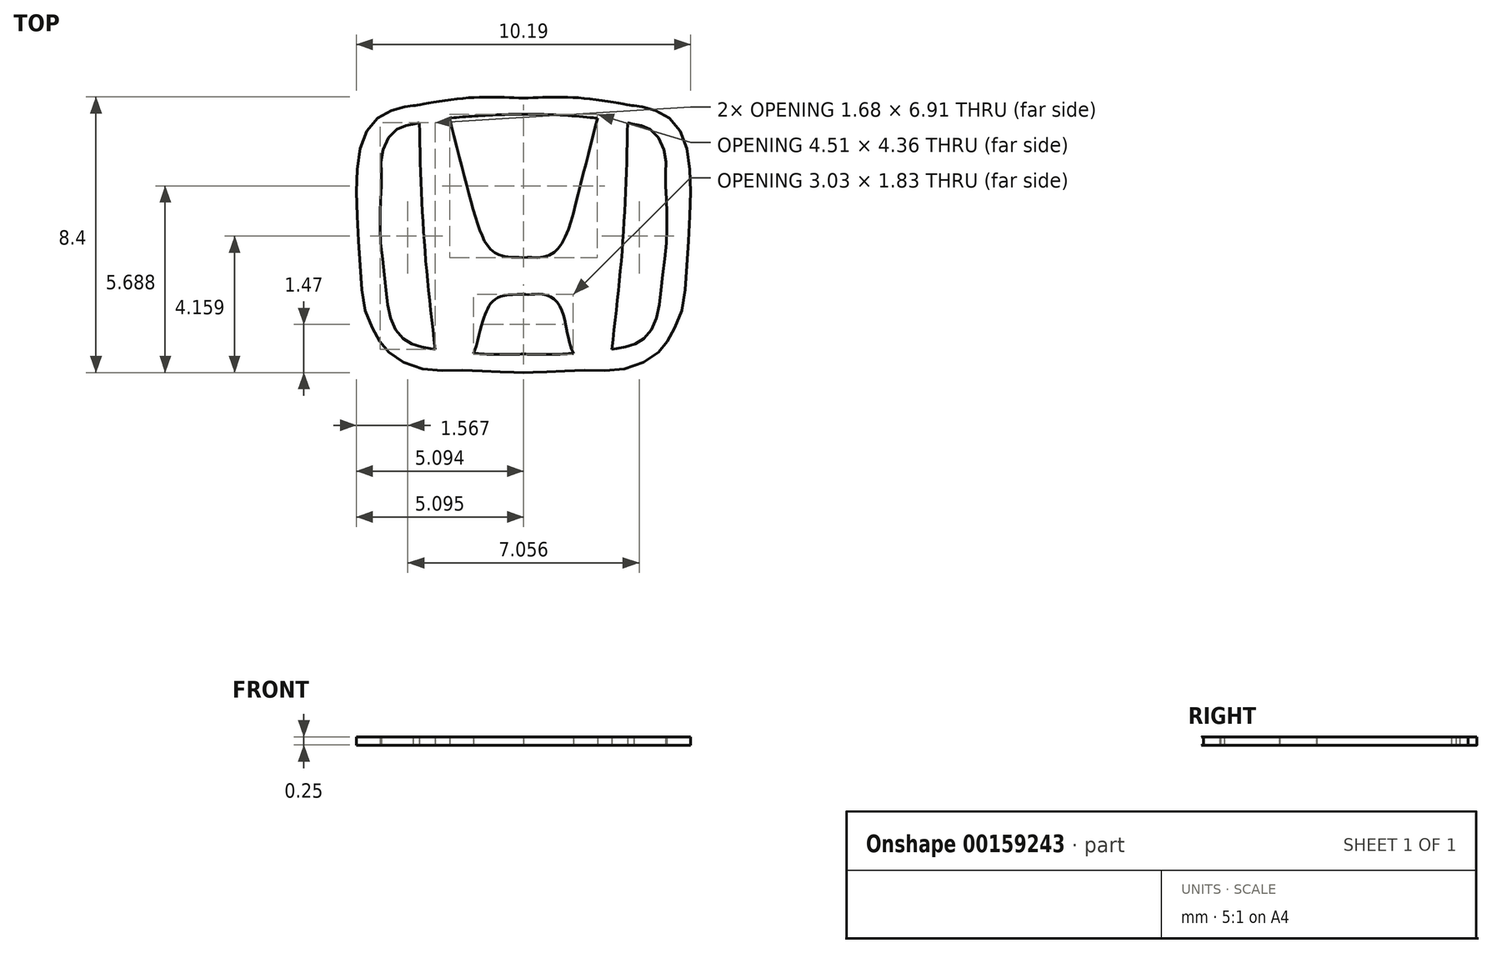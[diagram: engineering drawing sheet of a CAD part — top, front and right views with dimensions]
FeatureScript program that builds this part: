
annotation { "Feature Type Name" : "Feature", "Feature Type Description" : "" }
export const myFeature = defineFeature(function(context is Context, id is Id, definition is map)
    precondition{}
    {
        {
            var Q0;
            Q0=qCreatedBy(makeId("Top.planeOp"),FACE);
            var sketch = newSketch(context, id + "F0", { "sketchPlane" : qUnion([Q0])});
            skFitSpline(sketch, "E0.0", {"points": [v(1.68, -88.15) * mm, v(7.08, -88.08) * mm, v(18.75, -87.55) * mm, v(40.87, -86.74) * mm, v(64.03, -85.73) * mm, v(83.21, -76.44) * mm, v(90.57, -66.82) * mm, v(98.02, -50.85) * mm, v(101.38, -20.58) * mm, v(103.43, 15.7) * mm, v(101.94, 44.93) * mm, v(94.34, 63.37) * mm, v(81.86, 71.73) * mm, v(72.08, 74.1) * mm, v(68.98, 74.5) * mm]});
            skFitSpline(sketch, "E0.1", {"points": [v(65.18, 64.17) * mm, v(65.45, 64.1) * mm, v(70.48, 62.9) * mm, v(79.31, 60) * mm, v(87.76, 46.3) * mm, v(88.28, 32.38) * mm, v(88.84, 14.52) * mm, v(88.82, -7.63) * mm, v(85.9, -33.34) * mm, v(83.03, -54.06) * mm, v(75.44, -67.13) * mm, v(65.61, -72.1) * mm, v(58.1, -73.63) * mm, v(55.47, -74.06) * mm]});
            skFitSpline(sketch, "E0.2", {"points": [v(65.18, 64.17) * mm, v(63.78, 18) * mm, v(60.54, -28.08) * mm, v(55.47, -74.06) * mm]});
            skFitSpline(sketch, "E0.3", {"points": [v(1.68, -40.48) * mm, v(4.74, -40.57) * mm, v(11.56, -40.33) * mm, v(20.1, -43.16) * mm, v(26.16, -53.22) * mm, v(28.54, -64.7) * mm, v(30.94, -73.54) * mm, v(32.03, -76.46) * mm]});
            skFitSpline(sketch, "E0.4", {"points": [v(32.03, -76.46) * mm, v(21.9, -77) * mm, v(11.71, -77) * mm, v(1.68, -76.86) * mm]});
            skFitSpline(sketch, "E0.5", {"points": [v(1.68, -76.86) * mm, v(-8.35, -77) * mm, v(-18.53, -77) * mm, v(-28.67, -76.47) * mm]});
            skFitSpline(sketch, "E0.6", {"points": [v(-65.62, 74.5) * mm, v(-68.71, 74.1) * mm, v(-78.5, 71.73) * mm, v(-90.97, 63.37) * mm, v(-98.58, 44.93) * mm, v(-100.06, 15.7) * mm, v(-98, -20.58) * mm, v(-94.65, -50.85) * mm, v(-87.2, -66.82) * mm, v(-79.84, -76.44) * mm, v(-60.66, -85.73) * mm, v(-37.5, -86.74) * mm, v(-15.38, -87.55) * mm, v(-3.71, -88.08) * mm, v(1.68, -88.15) * mm]});
            skFitSpline(sketch, "E0.7", {"points": [v(1.68, -40.48) * mm, v(0.74, -40.5) * mm, v(-1.34, -40.52) * mm, v(-4.78, -40.58) * mm, v(-8.34, -40.87) * mm, v(-11.22, -41.45) * mm, v(-13.36, -42.2) * mm, v(-14.86, -42.94) * mm, v(-16.22, -43.86) * mm, v(-17.41, -45) * mm, v(-18.47, -46.3) * mm, v(-19.4, -47.74) * mm, v(-20.22, -49.25) * mm, v(-20.96, -50.8) * mm, v(-21.64, -52.36) * mm, v(-22.45, -54.47) * mm, v(-23.33, -57.13) * mm, v(-24.23, -60.35) * mm, v(-25.31, -64.67) * mm, v(-26.6, -70.09) * mm, v(-27.88, -74.36) * mm, v(-28.67, -76.47) * mm]});
            skFitSpline(sketch, "E0.8", {"points": [v(-52.1, -74.07) * mm, v(-57.18, -28.08) * mm, v(-60.41, 18) * mm, v(-61.8, 64.17) * mm]});
            skFitSpline(sketch, "E0.9", {"points": [v(-52.1, -74.07) * mm, v(-54.74, -73.63) * mm, v(-62.25, -72.1) * mm, v(-72.07, -67.13) * mm, v(-79.67, -54.06) * mm, v(-82.53, -33.34) * mm, v(-85.45, -7.63) * mm, v(-85.48, 14.52) * mm, v(-84.91, 32.38) * mm, v(-84.4, 46.3) * mm, v(-75.94, 60) * mm, v(-67.12, 62.9) * mm, v(-62.08, 64.1) * mm, v(-61.8, 64.17) * mm]});
            skFitSpline(sketch, "E0.10", {"points": [v(-43.39, 66.95) * mm, v(-42.32, 62.69) * mm, v(-40.72, 56.3) * mm, v(-38.56, 47.8) * mm, v(-36.93, 41.42) * mm, v(-35.3, 35.05) * mm, v(-33.65, 28.68) * mm, v(-32.26, 23.36) * mm, v(-31.15, 19.11) * mm, v(-30.02, 14.86) * mm, v(-28.86, 10.63) * mm, v(-27.59, 6.42) * mm, v(-26.57, 3.29) * mm, v(-25.48, 0.18) * mm, v(-24.5, -2.38) * mm, v(-23.65, -4.41) * mm, v(-22.77, -6.43) * mm, v(-21.78, -8.4) * mm, v(-20.62, -10.26) * mm, v(-19.63, -11.6) * mm, v(-18.53, -12.85) * mm, v(-17.32, -13.99) * mm, v(-16, -14.97) * mm, v(-14.57, -15.77) * mm, v(-13.05, -16.4) * mm, v(-10.93, -17.03) * mm, v(-8.14, -17.51) * mm, v(-4.71, -17.76) * mm, v(-1.36, -17.85) * mm, v(0.72, -17.93) * mm, v(1.7, -18) * mm]});
            skFitSpline(sketch, "E0.11", {"points": [v(46.76, 66.96) * mm, v(44.58, 58.2) * mm, v(40.64, 42.63) * mm, v(34.49, 18.89) * mm, v(29.82, 1.3) * mm, v(24.22, -10.6) * mm, v(19.3, -15.58) * mm, v(11.6, -17.99) * mm, v(5.08, -17.75) * mm, v(1.7, -18) * mm]});
            skFitSpline(sketch, "E0.12", {"points": [v(1.68, 69.24) * mm, v(8.06, 69.26) * mm, v(22.27, 68.9) * mm, v(37.32, 67.83) * mm, v(45.9, 67.04) * mm, v(46.76, 66.95) * mm]});
            skFitSpline(sketch, "E0.13", {"points": [v(-44.4, 66.82) * mm, v(-42.5, 67.01) * mm, v(-38.65, 67.37) * mm, v(-32.9, 67.84) * mm, v(-27.13, 68.26) * mm, v(-19.45, 68.73) * mm, v(-9.84, 69.13) * mm, v(-2.15, 69.25) * mm, v(1.69, 69.24) * mm]});
            skFitSpline(sketch, "E0.14", {"points": [v(1.68, 79.15) * mm, v(-16.64, 79.77) * mm, v(-39.11, 78.66) * mm, v(-61.36, 75.24) * mm, v(-65.62, 74.5) * mm]});
            skFitSpline(sketch, "E0.15", {"points": [v(68.98, 74.5) * mm, v(64.73, 75.24) * mm, v(42.48, 78.66) * mm, v(20, 79.77) * mm, v(1.68, 79.15) * mm]});
            skSolve(sketch);
        }
        {
            var Q0;
            Q0=makeQuery(id+"F0.imprint","IMPRINT",FACE,{"disambiguationData":[TD([[makeQuery(id+"F0.imprint","IMPRINT",EDGE,{"derivedFrom":sQuery(id+"F0.wireOp",EDGE,"E0.0")}),1.0]])]});
            extrude(context, id + "F1", {"entities" : qUnion([Q0]), "depth" : 5.08 * mm});
        }
        {
            var Q0;
            Q0=makeQuery(id+"F1.opExtrude","SWEPT_BODY",BODY,{"disambiguationData":[OSD([sQuery(id+"F0.wireOp",EDGE,"E0.0"),sQuery(id+"F0.wireOp",EDGE,"E0.1"),sQuery(id+"F0.wireOp",EDGE,"E0.2"),sQuery(id+"F0.wireOp",EDGE,"E0.3"),sQuery(id+"F0.wireOp",EDGE,"E0.4"),sQuery(id+"F0.wireOp",EDGE,"E0.5"),sQuery(id+"F0.wireOp",EDGE,"E0.6"),sQuery(id+"F0.wireOp",EDGE,"E0.7"),sQuery(id+"F0.wireOp",EDGE,"E0.8"),sQuery(id+"F0.wireOp",EDGE,"E0.9"),sQuery(id+"F0.wireOp",EDGE,"E0.10"),sQuery(id+"F0.wireOp",EDGE,"E0.11"),sQuery(id+"F0.wireOp",EDGE,"E0.12"),sQuery(id+"F0.wireOp",EDGE,"E0.13"),sQuery(id+"F0.wireOp",EDGE,"E0.14"),sQuery(id+"F0.wireOp",EDGE,"E0.15")])]});
            var Q1;
            Q1=makeQuery(id+"F1.opExtrude","CAP_VERTEX",VERTEX,{"disambiguationData":[OSD([sQuery(id+"F0.wireOp",EDGE,"E0.14"),sQuery(id+"F0.wireOp",EDGE,"E0.15")])],"isStart":false});
            transform(context, id + "F2", {"entities" : qUnion([Q0]), "transformType" : TransformType.SCALE_UNIFORMLY, "scale" : 0.05, "scalePoint" : qUnion([Q1]), "makeCopy" : false});
        }
    });
